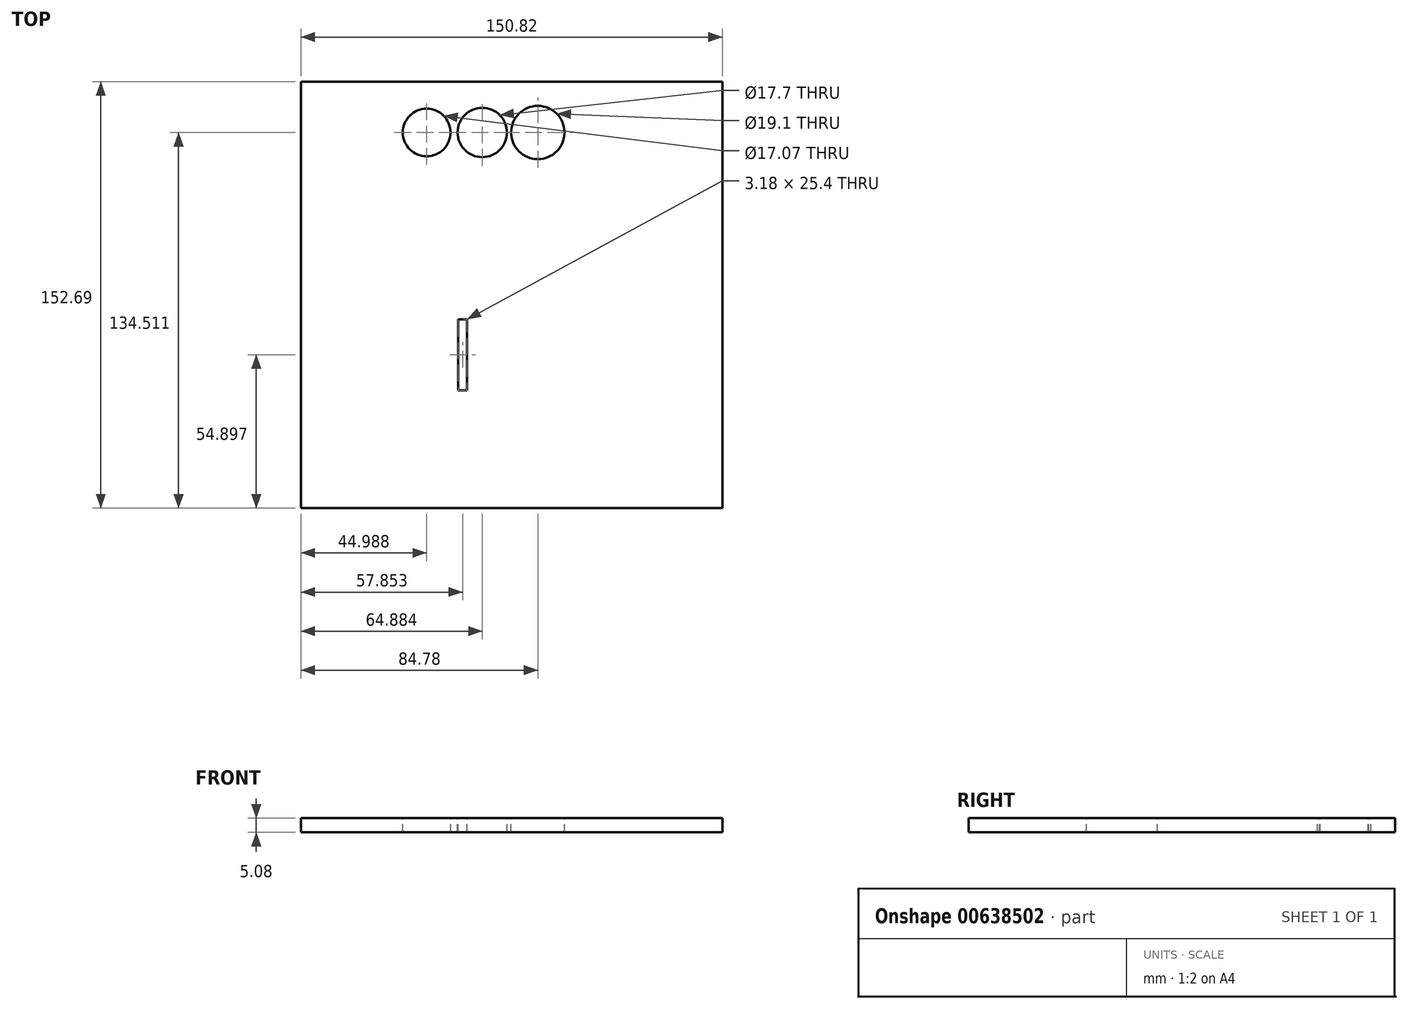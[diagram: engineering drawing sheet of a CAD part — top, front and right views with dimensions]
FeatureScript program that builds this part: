
annotation { "Feature Type Name" : "Feature", "Feature Type Description" : "" }
export const myFeature = defineFeature(function(context is Context, id is Id, definition is map)
    precondition{}
    {
        {
            var Q0;
            Q0=qCreatedBy(makeId("Top.planeOp"),FACE);
            var sketch = newSketch(context, id + "F0", { "sketchPlane" : qUnion([Q0])});
            skLineSegment(sketch, "E0.bottom", {"start": v(74.65, 75.72) * mm, "end": v(-76.17, 75.72) * mm});
            skLineSegment(sketch, "E0.top", {"start": v(74.65, -76.97) * mm, "end": v(-76.17, -76.97) * mm});
            skLineSegment(sketch, "E0.left", {"start": v(74.65, 75.72) * mm, "end": v(74.65, -76.97) * mm});
            skLineSegment(sketch, "E0.right", {"start": v(-76.17, 75.72) * mm, "end": v(-76.17, -76.97) * mm});
            skLineSegment(sketch, "E1", {"start": v(-31.18, 57.54) * mm, "end": v(8.6, 57.54) * mm});
            skPoint(sketch, "E2", {"position": v(-11.29, 57.54) * mm});
            skCircle(sketch, "E3", {"center": v(-11.29, 57.54) * mm, "radius": 8.85 * mm});
            skCircle(sketch, "E4", {"center": v(-31.18, 57.54) * mm, "radius": 8.54 * mm});
            skCircle(sketch, "E5", {"center": v(8.6, 57.54) * mm, "radius": 9.55 * mm});
            skLineSegment(sketch, "E6.bottom", {"start": v(-19.9, -9.37) * mm, "end": v(-16.73, -9.37) * mm});
            skLineSegment(sketch, "E6.top", {"start": v(-19.9, -34.77) * mm, "end": v(-16.73, -34.77) * mm});
            skLineSegment(sketch, "E6.left", {"start": v(-19.9, -9.37) * mm, "end": v(-19.9, -34.77) * mm});
            skLineSegment(sketch, "E6.right", {"start": v(-16.73, -9.37) * mm, "end": v(-16.73, -34.77) * mm});
            skSolve(sketch);
        }
        {
            var Q0;
            Q0 = qSketchRegion(id + "F0", true);
            extrude(context, id + "F1", {"entities" : qUnion([Q0]), "oppositeDirection" : true, "depth" : 5.08 * mm, "offsetDistance" : 25.4 * mm});
        }
    });
